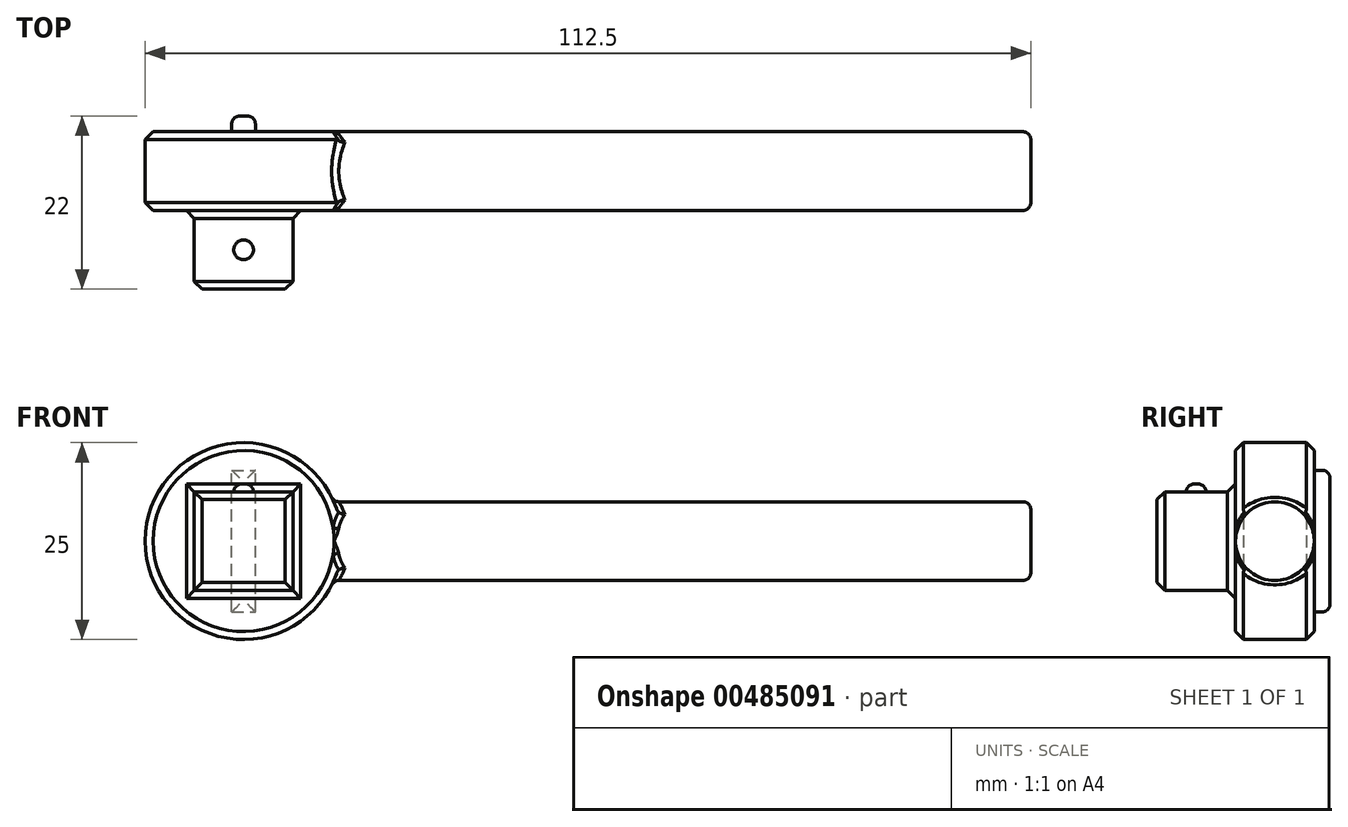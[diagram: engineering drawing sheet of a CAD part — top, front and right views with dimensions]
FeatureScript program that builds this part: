
annotation { "Feature Type Name" : "Feature", "Feature Type Description" : "" }
export const myFeature = defineFeature(function(context is Context, id is Id, definition is map)
    precondition{}
    {
        {
            var Q0;
            Q0=qCreatedBy(makeId("Front.planeOp"),FACE);
            var sketch = newSketch(context, id + "F0", { "sketchPlane" : qUnion([Q0])});
            skCircle(sketch, "E0", {"center": v(0, 0) * mm, "radius": 12.5 * mm});
            skSolve(sketch);
        }
        {
            var Q0;
            Q0 = qSketchRegion(id + "F0", true);
            extrude(context, id + "F1", {"entities" : qUnion([Q0]), "depth" : 10 * mm});
        }
        {
            var Q0;
            Q0=qCreatedBy(makeId("Right.planeOp"),FACE);
            var sketch = newSketch(context, id + "F2", { "sketchPlane" : qUnion([Q0])});
            skCircle(sketch, "E1", {"center": v(-5, 0) * mm, "radius": 5 * mm});
            skSolve(sketch);
        }
        {
            var Q0;
            Q0 = qSketchRegion(id + "F2", true);
            extrude(context, id + "F3", {"entities" : qUnion([Q0]), "operationType" : NewBodyOperationType.ADD, "depth" : 100 * mm});
        }
        {
            var Q0;
            Q0=makeQuery(id+"F1.opExtrude","CAP_FACE",FACE,{"disambiguationData":[OSD([sQuery(id+"F0.wireOp",EDGE,"E0")])],"isStart":false});
            var sketch = newSketch(context, id + "F4", { "sketchPlane" : qUnion([Q0])});
            skLineSegment(sketch, "E2.bottom", {"start": v(6.26, -6.26) * mm, "end": v(-6.26, -6.26) * mm});
            skLineSegment(sketch, "E2.top", {"start": v(6.26, 6.26) * mm, "end": v(-6.26, 6.26) * mm});
            skLineSegment(sketch, "E2.left", {"start": v(6.26, -6.26) * mm, "end": v(6.26, 6.26) * mm});
            skLineSegment(sketch, "E2.right", {"start": v(-6.26, -6.26) * mm, "end": v(-6.26, 6.26) * mm});
            skPoint(sketch, "E2.middle", {"position": v(0, 0) * mm});
            skSolve(sketch);
        }
        {
            var Q0;
            Q0 = qSketchRegion(id + "F4", true);
            extrude(context, id + "F5", {"entities" : qUnion([Q0]), "operationType" : NewBodyOperationType.ADD, "depth" : 10 * mm});
        }
        {
            var Q0;
            Q0=makeQuery(id+"F1.opExtrude","CAP_FACE",FACE,{"disambiguationData":[OSD([sQuery(id+"F0.wireOp",EDGE,"E0")])],"isStart":false});
            var Q1;
            Q1=makeQuery(id+"F5.opExtrude","CAP_FACE",FACE,{"disambiguationData":[OSD([sQuery(id+"F4.wireOp",EDGE,"E2.bottom"),sQuery(id+"F4.wireOp",EDGE,"E2.top"),sQuery(id+"F4.wireOp",EDGE,"E2.left"),sQuery(id+"F4.wireOp",EDGE,"E2.right")])],"isStart":false});
            var Q2;
            Q2=makeQuery(id+"F1.opExtrude","CAP_FACE",FACE,{"disambiguationData":[OSD([sQuery(id+"F0.wireOp",EDGE,"E0")])],"isStart":true});
            chamfer(context, id + "F6", {"entities" : qUnion([Q0, Q1, Q2]), "width" : 1 * mm, "tangentPropagation" : true});
        }
        {
            var Q0;
            Q0=makeQuery(id+"F3.opExtrude","SWEPT_FACE",FACE,{"disambiguationData":[OSD([sQuery(id+"F2.wireOp",EDGE,"E1")])]});
            fillet(context, id + "F7", {"entities" : qUnion([Q0]), "radius" : 1 * mm, "tangentPropagation" : true, "allowEdgeOverflow" : false});
        }
        {
            var Q0;
            Q0=makeQuery(id+"F1.opExtrude","CAP_FACE",FACE,{"disambiguationData":[OSD([sQuery(id+"F0.wireOp",EDGE,"E0")])],"isStart":true});
            var sketch = newSketch(context, id + "F8", { "sketchPlane" : qUnion([Q0])});
            skLineSegment(sketch, "E3.bottom", {"start": v(1.5, -9) * mm, "end": v(-1.5, -9) * mm});
            skLineSegment(sketch, "E3.top", {"start": v(1.5, 9) * mm, "end": v(-1.5, 9) * mm});
            skLineSegment(sketch, "E3.left", {"start": v(1.5, -9) * mm, "end": v(1.5, 9) * mm});
            skLineSegment(sketch, "E3.right", {"start": v(-1.5, -9) * mm, "end": v(-1.5, 9) * mm});
            skPoint(sketch, "E3.middle", {"position": v(0, 0) * mm});
            skSolve(sketch);
        }
        {
            var Q0;
            Q0 = qSketchRegion(id + "F8", true);
            extrude(context, id + "F9", {"entities" : qUnion([Q0]), "operationType" : NewBodyOperationType.ADD, "depth" : 2 * mm});
        }
        {
            var Q0;
            Q0=makeQuery(id+"F9.opExtrude","CAP_FACE",FACE,{"disambiguationData":[OSD([sQuery(id+"F8.wireOp",EDGE,"E3.bottom"),sQuery(id+"F8.wireOp",EDGE,"E3.top"),sQuery(id+"F8.wireOp",EDGE,"E3.left"),sQuery(id+"F8.wireOp",EDGE,"E3.right")])],"isStart":false});
            fillet(context, id + "F10", {"entities" : qUnion([Q0]), "radius" : 1 * mm, "tangentPropagation" : true, "allowEdgeOverflow" : false});
        }
        {
            var Q0;
            Q0=makeQuery(id+"F5.opExtrude","SWEPT_FACE",FACE,{"disambiguationData":[OSD([sQuery(id+"F4.wireOp",EDGE,"E2.top")])]});
            var sketch = newSketch(context, id + "F11", { "sketchPlane" : qUnion([Q0])});
            skCircle(sketch, "E4", {"center": v(0, -15) * mm, "radius": 1.25 * mm});
            skPoint(sketch, "E4.centerSnap0", {"position": v(6.26, -15) * mm});
            skSolve(sketch);
        }
        {
            var Q0;
            Q0 = qSketchRegion(id + "F11", true);
            extrude(context, id + "F12", {"entities" : qUnion([Q0]), "operationType" : NewBodyOperationType.ADD, "depth" : 1 * mm});
        }
        {
            var Q0;
            Q0=makeQuery(id+"F12.opExtrude","CAP_EDGE",EDGE,{"disambiguationData":[OSD([sQuery(id+"F11.wireOp",EDGE,"E4")])],"isStart":false});
            fillet(context, id + "F13", {"entities" : qUnion([Q0]), "radius" : 1 * mm, "tangentPropagation" : true, "allowEdgeOverflow" : false});
        }
    });
